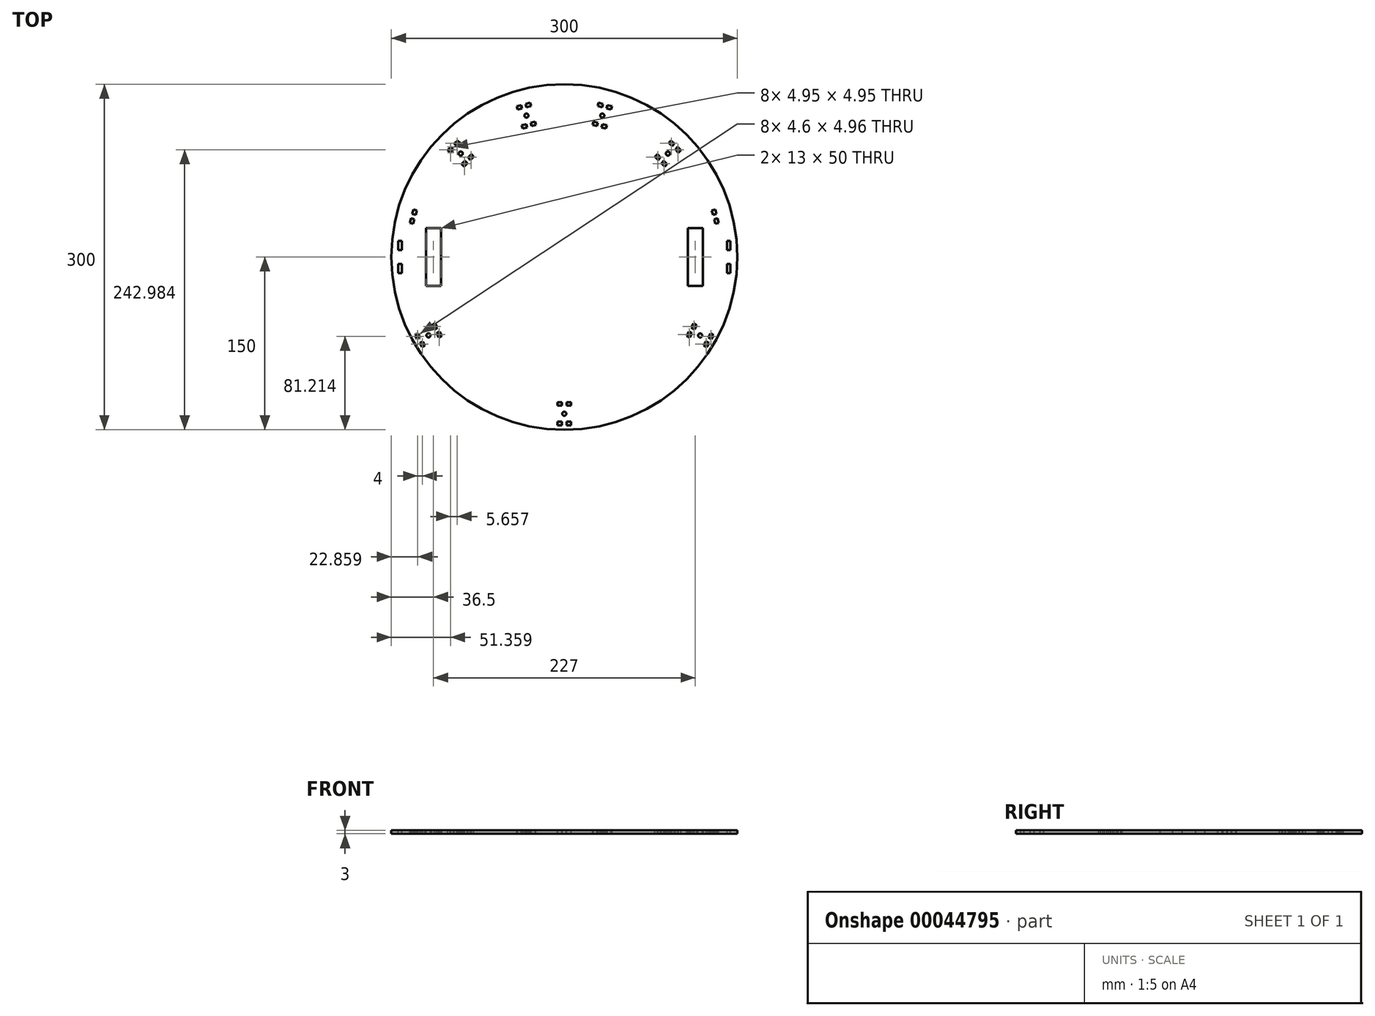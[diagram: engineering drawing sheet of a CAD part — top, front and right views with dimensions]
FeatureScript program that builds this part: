
annotation { "Feature Type Name" : "Feature", "Feature Type Description" : "" }
export const myFeature = defineFeature(function(context is Context, id is Id, definition is map)
    precondition{}
    {
        {
            var Q0;
            Q0=qCreatedBy(makeId("Top.planeOp"),FACE);
            var sketch = newSketch(context, id + "F0", { "sketchPlane" : qUnion([Q0])});
            skCircle(sketch, "E0", {"center": v(0, 0) * mm, "radius": 150 * mm});
            skLineSegment(sketch, "E1", {"start": v(0, 150) * mm, "end": v(0, -150) * mm, "construction": true});
            skLineSegment(sketch, "E2.bottom", {"start": v(-120, 25) * mm, "end": v(-107, 25) * mm});
            skLineSegment(sketch, "E2.top", {"start": v(-120, -25) * mm, "end": v(-107, -25) * mm});
            skLineSegment(sketch, "E2.left", {"start": v(-120, 25) * mm, "end": v(-120, -25) * mm});
            skLineSegment(sketch, "E2.right", {"start": v(-107, 25) * mm, "end": v(-107, -25) * mm});
            skLineSegment(sketch, "E3.bottom", {"start": v(-144, -6) * mm, "end": v(-141, -6) * mm});
            skLineSegment(sketch, "E3.top", {"start": v(-144, -14) * mm, "end": v(-141, -14) * mm});
            skLineSegment(sketch, "E3.left", {"start": v(-144, -6) * mm, "end": v(-144, -14) * mm});
            skLineSegment(sketch, "E3.right", {"start": v(-141, -6) * mm, "end": v(-141, -14) * mm});
            skLineSegment(sketch, "E4", {"start": v(150, 0) * mm, "end": v(-150, 0) * mm, "construction": true});
            skPoint(sketch, "E5", {"position": v(-107, 0) * mm});
            skLineSegment(sketch, "E6.MirrorCS", {"start": v(-144, 14) * mm, "end": v(-141, 14) * mm});
            skLineSegment(sketch, "E7.MirrorCS", {"start": v(-141, 6) * mm, "end": v(-141, 14) * mm});
            skLineSegment(sketch, "E8.MirrorCS", {"start": v(-144, 6) * mm, "end": v(-144, 14) * mm});
            skLineSegment(sketch, "E9.MirrorCS", {"start": v(-144, 6) * mm, "end": v(-141, 6) * mm});
            skLineSegment(sketch, "E10.MirrorCS", {"start": v(144, 6) * mm, "end": v(141, 6) * mm});
            skLineSegment(sketch, "E11.MirrorCS", {"start": v(144, 14) * mm, "end": v(141, 14) * mm});
            skLineSegment(sketch, "E12.MirrorCS", {"start": v(144, -6) * mm, "end": v(141, -6) * mm});
            skLineSegment(sketch, "E13.MirrorCS", {"start": v(144, -14) * mm, "end": v(141, -14) * mm});
            skLineSegment(sketch, "E14.MirrorCS", {"start": v(144, -6) * mm, "end": v(144, -14) * mm});
            skLineSegment(sketch, "E15.MirrorCS", {"start": v(141, -6) * mm, "end": v(141, -14) * mm});
            skLineSegment(sketch, "E16.MirrorCS", {"start": v(144, 6) * mm, "end": v(144, 14) * mm});
            skLineSegment(sketch, "E17.MirrorCS", {"start": v(107, 25) * mm, "end": v(107, -25) * mm});
            skLineSegment(sketch, "E18.MirrorCS", {"start": v(120, 25) * mm, "end": v(120, -25) * mm});
            skLineSegment(sketch, "E19.MirrorCS", {"start": v(120, -25) * mm, "end": v(107, -25) * mm});
            skLineSegment(sketch, "E20.MirrorCS", {"start": v(120, 25) * mm, "end": v(107, 25) * mm});
            skPoint(sketch, "E21.MirrorP", {"position": v(107, 0) * mm});
            skLineSegment(sketch, "E22.MirrorCS", {"start": v(141, 6) * mm, "end": v(141, 14) * mm});
            skSolve(sketch);
        }
        {
            var Q0;
            Q0=makeQuery(id+"F0.imprint","IMPRINT",FACE,{"disambiguationData":[TD([[makeQuery(id+"F0.imprint","IMPRINT",EDGE,{"derivedFrom":sQuery(id+"F0.wireOp",EDGE,"E0")}),1.0]])]});
            extrude(context, id + "F1", {"entities" : qUnion([Q0]), "oppositeDirection" : true, "depth" : 3 * mm});
        }
        {
            var Q0;
            Q0=makeQuery(id+"F1.opExtrude","CAP_FACE",FACE,{"disambiguationData":[OSD([sQuery(id+"F0.wireOp",EDGE,"E0"),sQuery(id+"F0.wireOp",EDGE,"E2.bottom"),sQuery(id+"F0.wireOp",EDGE,"E2.top"),sQuery(id+"F0.wireOp",EDGE,"E2.left"),sQuery(id+"F0.wireOp",EDGE,"E2.right"),sQuery(id+"F0.wireOp",EDGE,"E3.bottom"),sQuery(id+"F0.wireOp",EDGE,"E3.top"),sQuery(id+"F0.wireOp",EDGE,"E3.left"),sQuery(id+"F0.wireOp",EDGE,"E3.right"),sQuery(id+"F0.wireOp",EDGE,"cbf36644-4c9d-44f4-99aa-729f08500aa81.MirrorCS"),sQuery(id+"F0.wireOp",EDGE,"cbf36644-4c9d-44f4-99aa-729f08500aa82.MirrorCS"),sQuery(id+"F0.wireOp",EDGE,"cbf36644-4c9d-44f4-99aa-729f08500aa83.MirrorCS"),sQuery(id+"F0.wireOp",EDGE,"cbf36644-4c9d-44f4-99aa-729f08500aa84.MirrorCS"),sQuery(id+"F0.wireOp",EDGE,"868d1104-2d39-4a06-ab7a-803dcc4c7a7c1.MirrorCS"),sQuery(id+"F0.wireOp",EDGE,"868d1104-2d39-4a06-ab7a-803dcc4c7a7c2.MirrorCS"),sQuery(id+"F0.wireOp",EDGE,"868d1104-2d39-4a06-ab7a-803dcc4c7a7c3.MirrorCS"),sQuery(id+"F0.wireOp",EDGE,"868d1104-2d39-4a06-ab7a-803dcc4c7a7c4.MirrorCS")])],"isStart":true});
            var sketch = newSketch(context, id + "F2", { "sketchPlane" : qUnion([Q0])});
            skCircle(sketch, "E23.0", {"center": v(0, 0) * mm, "radius": 150 * mm, "construction": true});
            skLineSegment(sketch, "E24.1", {"start": v(0, 150) * mm, "end": v(0, -150) * mm, "construction": true});
            skLineSegment(sketch, "E25.2", {"start": v(150, 0) * mm, "end": v(-150, 0) * mm, "construction": true});
            skCircle(sketch, "E26.0", {"center": v(0, 0) * mm, "radius": 151 * mm, "construction": true});
            skCircle(sketch, "E27.0", {"center": v(0, 0) * mm, "radius": 154 * mm, "construction": true});
            skLineSegment(sketch, "E28", {"start": v(0, 150) * mm, "end": v(0, 151) * mm, "construction": true});
            skLineSegment(sketch, "E29", {"start": v(0, 151) * mm, "end": v(0, 154) * mm, "construction": true});
            skLineSegment(sketch, "E30", {"start": v(0, 0) * mm, "end": v(-75, 129.9) * mm, "construction": true});
            skLineSegment(sketch, "E31", {"start": v(-75, 129.9) * mm, "end": v(-75.5, 130.77) * mm, "construction": true});
            skLineSegment(sketch, "E32", {"start": v(-75.5, 130.77) * mm, "end": v(-77, 133.37) * mm, "construction": true});
            skLineSegment(sketch, "E33", {"start": v(0, 0) * mm, "end": v(-150, 0) * mm, "construction": true});
            skLineSegment(sketch, "E34", {"start": v(-150, 0) * mm, "end": v(-151, 0) * mm, "construction": true});
            skLineSegment(sketch, "E35", {"start": v(-151, 0) * mm, "end": v(-154, 0) * mm, "construction": true});
            skLineSegment(sketch, "E36", {"start": v(0, 0) * mm, "end": v(-38.82, 144.89) * mm, "construction": true});
            skLineSegment(sketch, "E37", {"start": v(-38.82, 144.89) * mm, "end": v(-39.08, 145.85) * mm, "construction": true});
            skLineSegment(sketch, "E38", {"start": v(-39.08, 145.85) * mm, "end": v(-39.86, 148.75) * mm, "construction": true});
            skLineSegment(sketch, "E39", {"start": v(-41.25, 130.78) * mm, "end": v(-37.4, 131.81) * mm});
            skLineSegment(sketch, "E40", {"start": v(-37.4, 131.81) * mm, "end": v(-36.61, 128.92) * mm});
            skLineSegment(sketch, "E41", {"start": v(-36.61, 128.92) * mm, "end": v(-40.48, 127.88) * mm});
            skLineSegment(sketch, "E42", {"start": v(-40.48, 127.88) * mm, "end": v(-41.25, 130.78) * mm});
            skLineSegment(sketch, "E43", {"start": v(-33, 115.4) * mm, "end": v(-36.85, 114.36) * mm});
            skLineSegment(sketch, "E44", {"start": v(-36.85, 114.36) * mm, "end": v(-36.08, 111.46) * mm});
            skLineSegment(sketch, "E45", {"start": v(-36.08, 111.46) * mm, "end": v(-32.21, 112.5) * mm});
            skLineSegment(sketch, "E46", {"start": v(-33, 115.4) * mm, "end": v(-32.21, 112.5) * mm});
            skCircle(sketch, "E47", {"center": v(-32.87, 122.67) * mm, "radius": 1.75 * mm});
            skLineSegment(sketch, "E48.MirrorCS", {"start": v(-29.66, 133.88) * mm, "end": v(-33.53, 132.85) * mm});
            skLineSegment(sketch, "E49.MirrorCS", {"start": v(-33.53, 132.85) * mm, "end": v(-32.75, 129.95) * mm});
            skLineSegment(sketch, "E50.MirrorCS", {"start": v(-32.75, 129.95) * mm, "end": v(-28.89, 130.99) * mm});
            skLineSegment(sketch, "E51.MirrorCS", {"start": v(-29.13, 116.43) * mm, "end": v(-25.26, 117.46) * mm});
            skLineSegment(sketch, "E52.MirrorCS", {"start": v(-29.13, 116.43) * mm, "end": v(-28.35, 113.53) * mm});
            skLineSegment(sketch, "E53.MirrorCS", {"start": v(-24.49, 114.57) * mm, "end": v(-28.35, 113.53) * mm});
            skLineSegment(sketch, "E54.MirrorCS", {"start": v(-25.26, 117.46) * mm, "end": v(-24.49, 114.57) * mm});
            skLineSegment(sketch, "E55.MirrorCS", {"start": v(-28.89, 130.99) * mm, "end": v(-29.66, 133.88) * mm});
            skLineSegment(sketch, "E56.anchor1", {"start": v(0, 0) * mm, "end": v(-32.87, 122.67) * mm, "construction": true});
            skLineSegment(sketch, "E57", {"start": v(0, 0) * mm, "end": v(-133.37, -77) * mm, "construction": true});
            skCircle(sketch, "E58", {"center": v(-117.78, -68) * mm, "radius": 1.75 * mm});
            skLineSegment(sketch, "E59", {"start": v(-110.72, -66.23) * mm, "end": v(-108.72, -69.7) * mm});
            skLineSegment(sketch, "E60", {"start": v(-122.84, -73.23) * mm, "end": v(-120.84, -76.7) * mm});
            skLineSegment(sketch, "E61", {"start": v(-125.44, -74.73) * mm, "end": v(-122.84, -73.23) * mm});
            skLineSegment(sketch, "E62", {"start": v(-110.72, -66.23) * mm, "end": v(-108.12, -64.73) * mm});
            skLineSegment(sketch, "E63", {"start": v(-106.12, -68.2) * mm, "end": v(-108.12, -64.73) * mm});
            skLineSegment(sketch, "E64", {"start": v(-123.44, -78.2) * mm, "end": v(-125.44, -74.73) * mm});
            skLineSegment(sketch, "E65", {"start": v(-108.72, -69.7) * mm, "end": v(-106.12, -68.2) * mm});
            skLineSegment(sketch, "E66", {"start": v(-120.84, -76.7) * mm, "end": v(-123.44, -78.2) * mm});
            skPoint(sketch, "E67", {"position": v(-130.77, -75.5) * mm});
            skLineSegment(sketch, "E68.MirrorCS", {"start": v(-112.72, -62.77) * mm, "end": v(-110.12, -61.27) * mm});
            skLineSegment(sketch, "E69.MirrorCS", {"start": v(-112.12, -57.8) * mm, "end": v(-110.12, -61.27) * mm});
            skLineSegment(sketch, "E70.MirrorCS", {"start": v(-114.72, -59.3) * mm, "end": v(-112.12, -57.8) * mm});
            skLineSegment(sketch, "E71.MirrorCS", {"start": v(-112.72, -62.77) * mm, "end": v(-114.72, -59.3) * mm});
            skLineSegment(sketch, "E72.MirrorCS", {"start": v(-124.84, -69.77) * mm, "end": v(-126.84, -66.3) * mm});
            skLineSegment(sketch, "E73.MirrorCS", {"start": v(-126.84, -66.3) * mm, "end": v(-129.44, -67.8) * mm});
            skLineSegment(sketch, "E74.MirrorCS", {"start": v(-127.44, -71.27) * mm, "end": v(-124.84, -69.77) * mm});
            skLineSegment(sketch, "E75.MirrorCS", {"start": v(-129.44, -67.8) * mm, "end": v(-127.44, -71.27) * mm});
            skLineSegment(sketch, "E76.MirrorCS", {"start": v(110.72, -66.23) * mm, "end": v(108.12, -64.73) * mm});
            skLineSegment(sketch, "E77.MirrorCS", {"start": v(110.72, -66.23) * mm, "end": v(108.72, -69.7) * mm});
            skLineSegment(sketch, "E78.MirrorCS", {"start": v(129.44, -67.8) * mm, "end": v(127.44, -71.27) * mm});
            skLineSegment(sketch, "E79.MirrorCS", {"start": v(127.44, -71.27) * mm, "end": v(124.84, -69.77) * mm});
            skLineSegment(sketch, "E80.MirrorCS", {"start": v(114.72, -59.3) * mm, "end": v(112.12, -57.8) * mm});
            skLineSegment(sketch, "E81.MirrorCS", {"start": v(112.12, -57.8) * mm, "end": v(110.12, -61.27) * mm});
            skLineSegment(sketch, "E82.MirrorCS", {"start": v(112.72, -62.77) * mm, "end": v(110.12, -61.27) * mm});
            skLineSegment(sketch, "E83.MirrorCS", {"start": v(112.72, -62.77) * mm, "end": v(114.72, -59.3) * mm});
            skLineSegment(sketch, "E84.MirrorCS", {"start": v(124.84, -69.77) * mm, "end": v(126.84, -66.3) * mm});
            skLineSegment(sketch, "E85.MirrorCS", {"start": v(126.84, -66.3) * mm, "end": v(129.44, -67.8) * mm});
            skLineSegment(sketch, "E86.MirrorCS", {"start": v(106.12, -68.2) * mm, "end": v(108.12, -64.73) * mm});
            skLineSegment(sketch, "E87.MirrorCS", {"start": v(108.72, -69.7) * mm, "end": v(106.12, -68.2) * mm});
            skCircle(sketch, "E88.MirrorC", {"center": v(117.78, -68) * mm, "radius": 1.75 * mm});
            skLineSegment(sketch, "E89.MirrorCS", {"start": v(125.44, -74.73) * mm, "end": v(122.84, -73.23) * mm});
            skLineSegment(sketch, "E90.MirrorCS", {"start": v(122.84, -73.23) * mm, "end": v(120.84, -76.7) * mm});
            skLineSegment(sketch, "E91.MirrorCS", {"start": v(123.44, -78.2) * mm, "end": v(125.44, -74.73) * mm});
            skLineSegment(sketch, "E92.MirrorCS", {"start": v(120.84, -76.7) * mm, "end": v(123.44, -78.2) * mm});
            skPoint(sketch, "E93.MirrorP", {"position": v(130.77, -75.5) * mm});
            skPoint(sketch, "E94.1.0", {"position": v(0, -151) * mm});
            skCircle(sketch, "E94.1.1", {"center": v(0, -136) * mm, "radius": 1.75 * mm});
            skPoint(sketch, "E94.1.2", {"position": v(0, -151) * mm});
            skLineSegment(sketch, "E94.1.3", {"start": v(6, -129) * mm, "end": v(6, -126) * mm});
            skLineSegment(sketch, "E94.1.4", {"start": v(-2, -129) * mm, "end": v(-2, -126) * mm});
            skLineSegment(sketch, "E94.1.5", {"start": v(6, -143) * mm, "end": v(6, -146) * mm});
            skLineSegment(sketch, "E94.1.6", {"start": v(-6, -129) * mm, "end": v(-6, -126) * mm});
            skLineSegment(sketch, "E94.1.7", {"start": v(-2, -143) * mm, "end": v(-6, -143) * mm});
            skLineSegment(sketch, "E94.1.8", {"start": v(-6, -143) * mm, "end": v(-6, -146) * mm});
            skLineSegment(sketch, "E94.1.9", {"start": v(-2, -146) * mm, "end": v(-2, -143) * mm});
            skLineSegment(sketch, "E94.1.10", {"start": v(6, -146) * mm, "end": v(2, -146) * mm});
            skLineSegment(sketch, "E94.1.11", {"start": v(2, -143) * mm, "end": v(6, -143) * mm});
            skLineSegment(sketch, "E94.1.12", {"start": v(2, -146) * mm, "end": v(2, -143) * mm});
            skLineSegment(sketch, "E94.1.13", {"start": v(-6, -146) * mm, "end": v(-2, -146) * mm});
            skLineSegment(sketch, "E94.1.14", {"start": v(2, -129) * mm, "end": v(6, -129) * mm});
            skLineSegment(sketch, "E94.1.15", {"start": v(6, -126) * mm, "end": v(2, -126) * mm});
            skLineSegment(sketch, "E94.1.16", {"start": v(2, -129) * mm, "end": v(2, -126) * mm});
            skLineSegment(sketch, "E94.1.17", {"start": v(-2, -129) * mm, "end": v(-6, -129) * mm});
            skLineSegment(sketch, "E94.1.18", {"start": v(-6, -126) * mm, "end": v(-2, -126) * mm});
            skLineSegment(sketch, "E94.anchor1", {"start": v(0, 0) * mm, "end": v(-130.77, -75.5) * mm, "construction": true});
            skLineSegment(sketch, "E94.anchor2", {"start": v(0, 0) * mm, "end": v(0, -151) * mm, "construction": true});
            skLineSegment(sketch, "E95.1.0", {"start": v(-86.97, 78.49) * mm, "end": v(-84.15, 81.32) * mm});
            skLineSegment(sketch, "E95.1.1", {"start": v(-89.1, 80.61) * mm, "end": v(-86.97, 78.49) * mm});
            skLineSegment(sketch, "E95.1.2", {"start": v(-86.27, 83.44) * mm, "end": v(-84.15, 81.32) * mm});
            skLineSegment(sketch, "E95.1.3", {"start": v(-83.44, 86.27) * mm, "end": v(-81.32, 84.15) * mm});
            skLineSegment(sketch, "E95.1.4", {"start": v(-78.49, 86.97) * mm, "end": v(-81.32, 84.15) * mm});
            skLineSegment(sketch, "E95.1.5", {"start": v(-86.27, 83.44) * mm, "end": v(-89.1, 80.61) * mm});
            skLineSegment(sketch, "E95.1.6", {"start": v(-80.61, 89.1) * mm, "end": v(-78.49, 86.97) * mm});
            skLineSegment(sketch, "E95.1.7", {"start": v(-83.44, 86.27) * mm, "end": v(-80.61, 89.1) * mm});
            skCircle(sketch, "E95.1.8", {"center": v(-89.8, 89.8) * mm, "radius": 1.75 * mm});
            skLineSegment(sketch, "E95.1.9", {"start": v(-99, 90.5) * mm, "end": v(-101.12, 92.63) * mm});
            skLineSegment(sketch, "E95.1.10", {"start": v(-96.17, 93.34) * mm, "end": v(-99, 90.5) * mm});
            skLineSegment(sketch, "E95.1.11", {"start": v(-98.29, 95.46) * mm, "end": v(-96.17, 93.34) * mm});
            skLineSegment(sketch, "E95.1.12", {"start": v(-93.34, 96.17) * mm, "end": v(-90.5, 99) * mm});
            skLineSegment(sketch, "E95.1.13", {"start": v(-101.12, 92.63) * mm, "end": v(-98.29, 95.46) * mm});
            skLineSegment(sketch, "E95.1.14", {"start": v(-95.46, 98.29) * mm, "end": v(-93.34, 96.17) * mm});
            skLineSegment(sketch, "E95.1.15", {"start": v(-90.5, 99) * mm, "end": v(-92.63, 101.12) * mm});
            skLineSegment(sketch, "E95.1.16", {"start": v(-92.63, 101.12) * mm, "end": v(-95.46, 98.29) * mm});
            skLineSegment(sketch, "E95.1.17", {"start": v(-106.07, 106.07) * mm, "end": v(-106.77, 106.77) * mm, "construction": true});
            skLineSegment(sketch, "E95.1.18", {"start": v(-106.77, 106.77) * mm, "end": v(-108.9, 108.9) * mm, "construction": true});
            skLineSegment(sketch, "E95.1.19", {"start": v(0, 0) * mm, "end": v(-106.07, 106.07) * mm, "construction": true});
            skLineSegment(sketch, "E95.anchor2", {"start": v(0, 0) * mm, "end": v(-89.8, 89.8) * mm, "construction": true});
            skLineSegment(sketch, "E96.1.0", {"start": v(-130.99, 28.89) * mm, "end": v(-133.88, 29.66) * mm});
            skLineSegment(sketch, "E96.1.1", {"start": v(-129.95, 32.75) * mm, "end": v(-130.99, 28.89) * mm});
            skLineSegment(sketch, "E96.1.2", {"start": v(-133.88, 29.66) * mm, "end": v(-132.85, 33.53) * mm});
            skLineSegment(sketch, "E96.1.3", {"start": v(-132.85, 33.53) * mm, "end": v(-129.95, 32.75) * mm});
            skLineSegment(sketch, "E96.1.4", {"start": v(-131.81, 37.4) * mm, "end": v(-128.92, 36.61) * mm});
            skLineSegment(sketch, "E96.1.5", {"start": v(-128.92, 36.61) * mm, "end": v(-127.88, 40.48) * mm});
            skLineSegment(sketch, "E96.1.6", {"start": v(-130.78, 41.25) * mm, "end": v(-131.81, 37.4) * mm});
            skLineSegment(sketch, "E96.1.7", {"start": v(-127.88, 40.48) * mm, "end": v(-130.78, 41.25) * mm});
            skLineSegment(sketch, "E96.1.8", {"start": v(0, 0) * mm, "end": v(-122.67, 32.87) * mm, "construction": true});
            skLineSegment(sketch, "E96.1.9", {"start": v(0, 0) * mm, "end": v(-144.89, 38.82) * mm, "construction": true});
            skLineSegment(sketch, "E96.1.10", {"start": v(-145.85, 39.08) * mm, "end": v(-148.75, 39.86) * mm, "construction": true});
            skLineSegment(sketch, "E96.1.11", {"start": v(-144.89, 38.82) * mm, "end": v(-145.85, 39.08) * mm, "construction": true});
            skLineSegment(sketch, "E96.anchor2", {"start": v(0, 0) * mm, "end": v(-122.67, 32.87) * mm, "construction": true});
            skLineSegment(sketch, "E97.MirrorCS", {"start": v(29.66, 133.88) * mm, "end": v(33.53, 132.85) * mm});
            skLineSegment(sketch, "E98.MirrorCS", {"start": v(28.89, 130.99) * mm, "end": v(29.66, 133.88) * mm});
            skLineSegment(sketch, "E99.MirrorCS", {"start": v(41.25, 130.78) * mm, "end": v(37.4, 131.81) * mm});
            skLineSegment(sketch, "E100.MirrorCS", {"start": v(33.53, 132.85) * mm, "end": v(32.75, 129.95) * mm});
            skLineSegment(sketch, "E101.MirrorCS", {"start": v(32.75, 129.95) * mm, "end": v(28.89, 130.99) * mm});
            skLineSegment(sketch, "E102.MirrorCS", {"start": v(37.4, 131.81) * mm, "end": v(36.61, 128.92) * mm});
            skLineSegment(sketch, "E103.MirrorCS", {"start": v(36.61, 128.92) * mm, "end": v(40.48, 127.88) * mm});
            skLineSegment(sketch, "E104.MirrorCS", {"start": v(40.48, 127.88) * mm, "end": v(41.25, 130.78) * mm});
            skLineSegment(sketch, "E105.MirrorCS", {"start": v(29.13, 116.43) * mm, "end": v(25.26, 117.46) * mm});
            skLineSegment(sketch, "E106.MirrorCS", {"start": v(25.26, 117.46) * mm, "end": v(24.49, 114.57) * mm});
            skLineSegment(sketch, "E107.MirrorCS", {"start": v(33, 115.4) * mm, "end": v(36.85, 114.36) * mm});
            skLineSegment(sketch, "E108.MirrorCS", {"start": v(29.13, 116.43) * mm, "end": v(28.35, 113.53) * mm});
            skLineSegment(sketch, "E109.MirrorCS", {"start": v(33, 115.4) * mm, "end": v(32.21, 112.5) * mm});
            skLineSegment(sketch, "E110.MirrorCS", {"start": v(36.85, 114.36) * mm, "end": v(36.08, 111.46) * mm});
            skCircle(sketch, "E111.MirrorC", {"center": v(32.87, 122.67) * mm, "radius": 1.75 * mm});
            skLineSegment(sketch, "E112.MirrorCS", {"start": v(24.49, 114.57) * mm, "end": v(28.35, 113.53) * mm});
            skLineSegment(sketch, "E113.MirrorCS", {"start": v(36.08, 111.46) * mm, "end": v(32.21, 112.5) * mm});
            skLineSegment(sketch, "E114.MirrorCS", {"start": v(95.46, 98.29) * mm, "end": v(93.34, 96.17) * mm});
            skLineSegment(sketch, "E115.MirrorCS", {"start": v(98.29, 95.46) * mm, "end": v(96.17, 93.34) * mm});
            skLineSegment(sketch, "E116.MirrorCS", {"start": v(101.12, 92.63) * mm, "end": v(98.29, 95.46) * mm});
            skLineSegment(sketch, "E117.MirrorCS", {"start": v(99, 90.5) * mm, "end": v(101.12, 92.63) * mm});
            skLineSegment(sketch, "E118.MirrorCS", {"start": v(80.61, 89.1) * mm, "end": v(78.49, 86.97) * mm});
            skLineSegment(sketch, "E119.MirrorCS", {"start": v(78.49, 86.97) * mm, "end": v(81.32, 84.15) * mm});
            skLineSegment(sketch, "E120.MirrorCS", {"start": v(83.44, 86.27) * mm, "end": v(81.32, 84.15) * mm});
            skLineSegment(sketch, "E121.MirrorCS", {"start": v(86.27, 83.44) * mm, "end": v(84.15, 81.32) * mm});
            skLineSegment(sketch, "E122.MirrorCS", {"start": v(86.27, 83.44) * mm, "end": v(89.1, 80.61) * mm});
            skLineSegment(sketch, "E123.MirrorCS", {"start": v(86.97, 78.49) * mm, "end": v(84.15, 81.32) * mm});
            skLineSegment(sketch, "E124.MirrorCS", {"start": v(89.1, 80.61) * mm, "end": v(86.97, 78.49) * mm});
            skLineSegment(sketch, "E125.MirrorCS", {"start": v(93.34, 96.17) * mm, "end": v(90.5, 99) * mm});
            skLineSegment(sketch, "E126.MirrorCS", {"start": v(96.17, 93.34) * mm, "end": v(99, 90.5) * mm});
            skCircle(sketch, "E127.MirrorC", {"center": v(89.8, 89.8) * mm, "radius": 1.75 * mm});
            skLineSegment(sketch, "E128.MirrorCS", {"start": v(83.44, 86.27) * mm, "end": v(80.61, 89.1) * mm});
            skLineSegment(sketch, "E129.MirrorCS", {"start": v(90.5, 99) * mm, "end": v(92.63, 101.12) * mm});
            skLineSegment(sketch, "E130.MirrorCS", {"start": v(92.63, 101.12) * mm, "end": v(95.46, 98.29) * mm});
            skLineSegment(sketch, "E131.MirrorCS", {"start": v(127.88, 40.48) * mm, "end": v(130.78, 41.25) * mm});
            skLineSegment(sketch, "E132.MirrorCS", {"start": v(128.92, 36.61) * mm, "end": v(127.88, 40.48) * mm});
            skLineSegment(sketch, "E133.MirrorCS", {"start": v(131.81, 37.4) * mm, "end": v(128.92, 36.61) * mm});
            skLineSegment(sketch, "E134.MirrorCS", {"start": v(132.85, 33.53) * mm, "end": v(129.95, 32.75) * mm});
            skLineSegment(sketch, "E135.MirrorCS", {"start": v(129.95, 32.75) * mm, "end": v(130.99, 28.89) * mm});
            skLineSegment(sketch, "E136.MirrorCS", {"start": v(130.99, 28.89) * mm, "end": v(133.88, 29.66) * mm});
            skLineSegment(sketch, "E137.MirrorCS", {"start": v(130.78, 41.25) * mm, "end": v(131.81, 37.4) * mm});
            skLineSegment(sketch, "E138.MirrorCS", {"start": v(133.88, 29.66) * mm, "end": v(132.85, 33.53) * mm});
            skSolve(sketch);
        }
        {
            var Q0;
            Q0 = qSketchRegion(id + "F2", true);
            extrude(context, id + "F3", {"entities" : qUnion([Q0]), "operationType" : NewBodyOperationType.REMOVE, "endBound" : BoundingType.UP_TO_NEXT, "oppositeDirection" : true, "depth" : 25 * mm});
        }
    });
